# Revit family: ITK_Розетка информационная GENERICA_Настенная_2 порта_IP20
name_source: partatom
category: Обобщенные модели
units: mm (PartAtom-declared; Revit-internal decimal feet)

## family parameters
Всегда вертикально = Да
Может служить основой для арматурных стержней = Нет
На основе рабочей плоскости = Нет
Общий = Нет
При загрузке вырезать с полостями = Нет
Размер круглого соединителя = Использовать диаметр
Тип детали = Нормальный
Точка расчета площади = Нет

## types (2) — shared parameters
ADSK_URL страницы изделия = https://generica.su
ADSK_Версия Revit = 2019
ADSK_Версия семейства = 1.0
ADSK_Группирование = I. ЩИТЫ И ПУЛЬТЫ
ADSK_Единица измерения = шт
ADSK_Завод-изготовитель = IEK
ADSK_Материал наименование = АБС-пластик
IEK_URL = https://generica.su
IEK_Описание = Используется для подключения оконечного оборудования пользователей на рабочих местах к информационной сети.
KSI_CMa_Строительные материалы = 01.7.14.03
URL = https://www.iek.ru
Высота = 27 мм
Глубина = 60 мм
Изготовитель = ITK
Материал = Окраска - RAL 9005
Степень защиты = IP20
Ширина = 62 мм
zero-valued in all types: ADSK_Масса

## per-type parameters (varying)
| type | ADSK_Код изделия | ADSK_Наименование | IEK_Цена за единицу |
| Категория 5E_FTP | CS2-1C5EF-22-G | Розетка инф. настенная RJ45 кат. 5Е FTP 2 порта GENERICA | 261.2 |
| Категория 5E_UTP | CS2-1C5EU-22-G | Розетка инф. настенная RJ45 кат. 5Е UTP 2 порта GENERICA | 194.39 |
